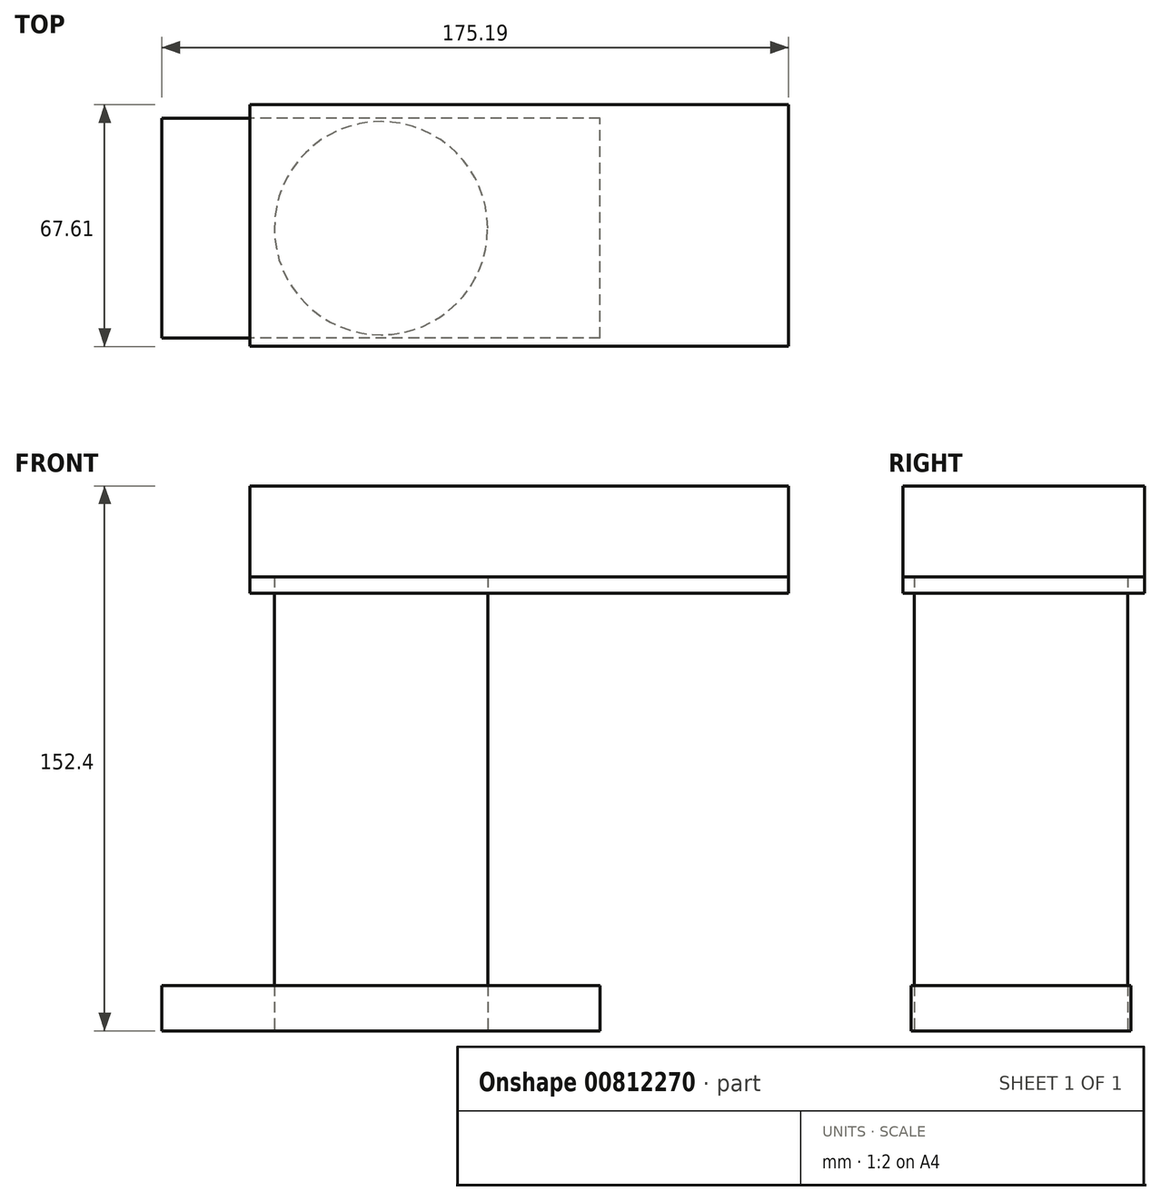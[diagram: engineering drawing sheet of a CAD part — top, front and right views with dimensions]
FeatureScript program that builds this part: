
annotation { "Feature Type Name" : "Feature", "Feature Type Description" : "" }
export const myFeature = defineFeature(function(context is Context, id is Id, definition is map)
    precondition{}
    {
        {
            var Q0;
            Q0=qCreatedBy(makeId("Top.planeOp"),FACE);
            var sketch = newSketch(context, id + "F0", { "sketchPlane" : qUnion([Q0])});
            skLineSegment(sketch, "E0.bottom", {"start": v(61.26, -30.7) * mm, "end": v(-61.26, -30.7) * mm});
            skLineSegment(sketch, "E0.top", {"start": v(61.26, 30.7) * mm, "end": v(-61.26, 30.7) * mm});
            skLineSegment(sketch, "E0.left", {"start": v(61.26, -30.7) * mm, "end": v(61.26, 30.7) * mm});
            skLineSegment(sketch, "E0.right", {"start": v(-61.26, -30.7) * mm, "end": v(-61.26, 30.7) * mm});
            skPoint(sketch, "E0.middle", {"position": v(0, 0) * mm});
            skSolve(sketch);
        }
        {
            var Q0;
            Q0=makeQuery(id+"F0.imprint","IMPRINT",FACE,{"disambiguationData":[TD([[makeQuery(id+"F0.imprint","IMPRINT",EDGE,{"derivedFrom":sQuery(id+"F0.wireOp",EDGE,"E0.bottom")}),-1.0]])]});
            extrude(context, id + "F1", {"entities" : qUnion([Q0]), "depth" : 12.7 * mm, "offsetDistance" : 25.4 * mm});
        }
        {
            var Q0;
            Q0=qCreatedBy(makeId("Top.planeOp"),FACE);
            var sketch = newSketch(context, id + "F2", { "sketchPlane" : qUnion([Q0])});
            skCircle(sketch, "E1", {"center": v(0, 0) * mm, "radius": 29.82 * mm});
            skSolve(sketch);
        }
        {
            var Q0;
            Q0 = qSketchRegion(id + "F2", true);
            var Q1;
            Q1=makeQuery(id+"F1.opExtrude","CAP_FACE",FACE,{"disambiguationData":[OSD([sQuery(id+"F0.wireOp",EDGE,"E0.bottom"),sQuery(id+"F0.wireOp",EDGE,"E0.top"),sQuery(id+"F0.wireOp",EDGE,"E0.left"),sQuery(id+"F0.wireOp",EDGE,"E0.right")])],"isStart":false});
            extrude(context, id + "F3", {"entities" : qUnion([Q0, Q1]), "depth" : 127 * mm, "offsetDistance" : 25.4 * mm});
        }
        {
            var Q0;
            Q0=makeQuery(id+"F3.opExtrude","SWEPT_BODY",BODY,{"disambiguationData":[OSD([sQuery(id+"F0.wireOp",EDGE,"E0.bottom"),sQuery(id+"F0.wireOp",EDGE,"E0.top"),sQuery(id+"F0.wireOp",EDGE,"E0.left"),sQuery(id+"F0.wireOp",EDGE,"E0.right")])]});
            deleteBodies(context, id + "F4", {"entities" : qUnion([Q0])});
        }
        {
            var Q0;
            Q0=makeQuery(id+"F3.opExtrude","CAP_FACE",FACE,{"disambiguationData":[OSD([sQuery(id+"F2.wireOp",EDGE,"E1")])],"isStart":false});
            var sketch = newSketch(context, id + "F5", { "sketchPlane" : qUnion([Q0])});
            skLineSegment(sketch, "E2.bottom", {"start": v(-36.68, 34.55) * mm, "end": v(113.93, 34.55) * mm});
            skLineSegment(sketch, "E2.top", {"start": v(-36.68, -33.06) * mm, "end": v(113.93, -33.06) * mm});
            skLineSegment(sketch, "E2.left", {"start": v(-36.68, 34.55) * mm, "end": v(-36.68, -33.06) * mm});
            skLineSegment(sketch, "E2.right", {"start": v(113.93, 34.55) * mm, "end": v(113.93, -33.06) * mm});
            skSolve(sketch);
        }
        {
            var Q0;
            Q0=makeQuery(id+"F5.imprint","IMPRINT",FACE,{"disambiguationData":[TD([[makeQuery(id+"F5.imprint","IMPRINT",EDGE,{"derivedFrom":makeQuery(id+"F3.opExtrude","CAP_EDGE",EDGE,{"disambiguationData":[OSD([sQuery(id+"F2.wireOp",EDGE,"E1")])],"isStart":false})}),1.0]])]});
            var Q1;
            Q1=makeQuery(id+"F5.imprint","IMPRINT",FACE,{"disambiguationData":[TD([[makeQuery(id+"F5.imprint","IMPRINT",EDGE,{"derivedFrom":sQuery(id+"F5.wireOp",EDGE,"E2.bottom")}),-1.0]])]});
            extrude(context, id + "F6", {"entities" : qUnion([Q0, Q1]), "oppositeDirection" : true, "depth" : 4.57 * mm, "offsetDistance" : 25.4 * mm});
        }
        {
            var Q0;
            Q0=makeQuery(id+"F6.opExtrude","CAP_FACE",FACE,{"disambiguationData":[OSD([sQuery(id+"F5.wireOp",EDGE,"E2.bottom"),sQuery(id+"F5.wireOp",EDGE,"E2.top"),sQuery(id+"F5.wireOp",EDGE,"E2.left"),sQuery(id+"F5.wireOp",EDGE,"E2.right")])],"isStart":true});
            extrude(context, id + "F7", {"entities" : qUnion([Q0]), "depth" : 25.4 * mm, "offsetDistance" : 25.4 * mm});
        }
    });
